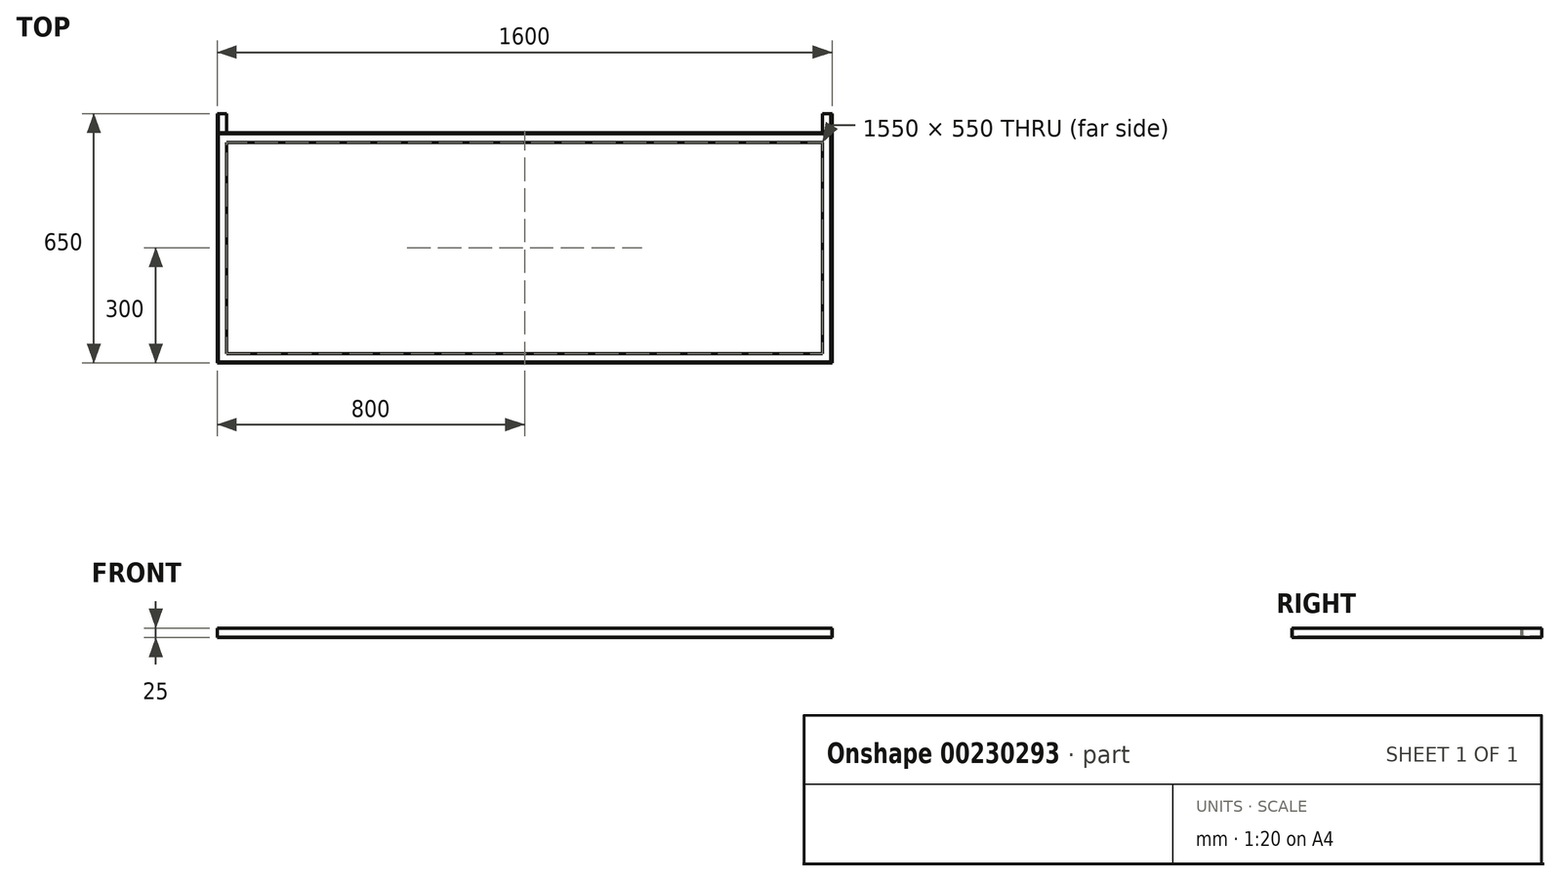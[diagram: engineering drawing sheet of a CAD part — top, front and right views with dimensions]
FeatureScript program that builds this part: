
annotation { "Feature Type Name" : "Feature", "Feature Type Description" : "" }
export const myFeature = defineFeature(function(context is Context, id is Id, definition is map)
    precondition{}
    {
        {
            var Q0;
            Q0=qCreatedBy(makeId("Right.planeOp"),FACE);
            var sketch = newSketch(context, id + "F0", { "sketchPlane" : qUnion([Q0])});
            skLineSegment(sketch, "E0", {"start": v(0, 0) * mm, "end": v(0, 25) * mm});
            skLineSegment(sketch, "E1", {"start": v(0, 25) * mm, "end": v(3, 25) * mm});
            skLineSegment(sketch, "E2", {"start": v(3, 25) * mm, "end": v(3, 3) * mm});
            skLineSegment(sketch, "E3", {"start": v(3, 3) * mm, "end": v(25, 3) * mm});
            skLineSegment(sketch, "E4", {"start": v(25, 3) * mm, "end": v(25, 0) * mm});
            skLineSegment(sketch, "E5", {"start": v(25, 0) * mm, "end": v(0, 0) * mm});
            skSolve(sketch);
        }
        {
            var Q0;
            Q0 = qSketchRegion(id + "F0", true);
            extrude(context, id + "F1", {"entities" : qUnion([Q0]), "depth" : 1600 * mm});
        }
        {
            var Q0;
            Q0=qCreatedBy(makeId("Front.planeOp"),FACE);
            var sketch = newSketch(context, id + "F2", { "sketchPlane" : qUnion([Q0])});
            skLineSegment(sketch, "E6", {"start": v(0, 0) * mm, "end": v(0, 25) * mm});
            skLineSegment(sketch, "E7", {"start": v(0, 25) * mm, "end": v(3, 25) * mm});
            skLineSegment(sketch, "E8", {"start": v(3, 25) * mm, "end": v(3, 3) * mm});
            skLineSegment(sketch, "E9", {"start": v(3, 3) * mm, "end": v(25, 3) * mm});
            skLineSegment(sketch, "E10", {"start": v(25, 3) * mm, "end": v(25, 0) * mm});
            skLineSegment(sketch, "E11", {"start": v(25, 0) * mm, "end": v(0, 0) * mm});
            skSolve(sketch);
        }
        {
            var Q0;
            Q0 = qSketchRegion(id + "F2", true);
            extrude(context, id + "F3", {"entities" : qUnion([Q0]), "operationType" : NewBodyOperationType.ADD, "oppositeDirection" : true, "depth" : 650 * mm});
        }
        {
            var Q0;
            Q0=qCreatedBy(makeId("Right.planeOp"),FACE);
            var sketch = newSketch(context, id + "F4", { "sketchPlane" : qUnion([Q0])});
            skLineSegment(sketch, "E12", {"start": v(600, 25) * mm, "end": v(600, 0) * mm});
            skLineSegment(sketch, "E13", {"start": v(600, 0) * mm, "end": v(575, 0) * mm});
            skLineSegment(sketch, "E14", {"start": v(575, 0) * mm, "end": v(575, 3) * mm});
            skLineSegment(sketch, "E15", {"start": v(575, 3) * mm, "end": v(597, 3) * mm});
            skLineSegment(sketch, "E16", {"start": v(597, 3) * mm, "end": v(597, 25) * mm});
            skLineSegment(sketch, "E17", {"start": v(597, 25) * mm, "end": v(600, 25) * mm});
            skSolve(sketch);
        }
        {
            var Q0;
            Q0 = qSketchRegion(id + "F4", true);
            extrude(context, id + "F5", {"entities" : qUnion([Q0]), "operationType" : NewBodyOperationType.ADD, "depth" : 1600 * mm});
        }
        {
            var Q0;
            Q0=qCreatedBy(makeId("Front.planeOp"),FACE);
            var sketch = newSketch(context, id + "F6", { "sketchPlane" : qUnion([Q0])});
            skLineSegment(sketch, "E18", {"start": v(1600, 25) * mm, "end": v(1600, 0) * mm});
            skLineSegment(sketch, "E19", {"start": v(1600, 0) * mm, "end": v(1575, 0) * mm});
            skLineSegment(sketch, "E20", {"start": v(1575, 0) * mm, "end": v(1575, 3) * mm});
            skLineSegment(sketch, "E21", {"start": v(1575, 3) * mm, "end": v(1597, 3) * mm});
            skLineSegment(sketch, "E22", {"start": v(1597, 3) * mm, "end": v(1597, 25) * mm});
            skLineSegment(sketch, "E23", {"start": v(1597, 25) * mm, "end": v(1600, 25) * mm});
            skSolve(sketch);
        }
        {
            var Q0;
            Q0 = qSketchRegion(id + "F6", true);
            extrude(context, id + "F7", {"entities" : qUnion([Q0]), "operationType" : NewBodyOperationType.ADD, "oppositeDirection" : true, "depth" : 650 * mm});
        }
    });
